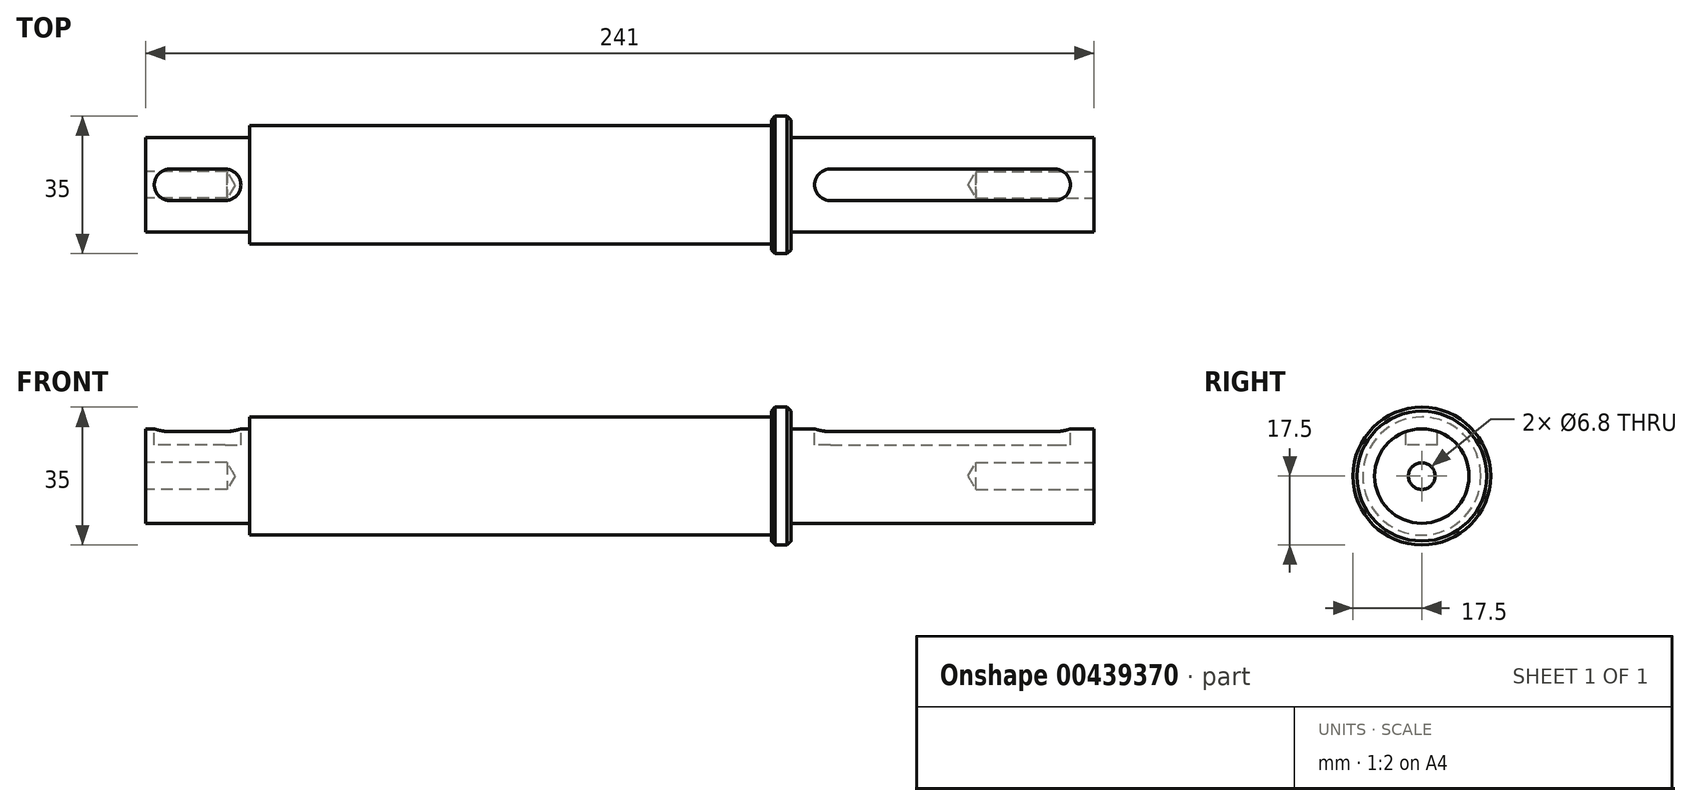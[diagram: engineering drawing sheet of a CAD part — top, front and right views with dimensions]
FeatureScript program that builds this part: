
annotation { "Feature Type Name" : "Feature", "Feature Type Description" : "" }
export const myFeature = defineFeature(function(context is Context, id is Id, definition is map)
    precondition{}
    {
        {
            var Q0;
            Q0=qCreatedBy(makeId("Right.planeOp"),FACE);
            var sketch = newSketch(context, id + "F0", { "sketchPlane" : qUnion([Q0])});
            skCircle(sketch, "E0", {"center": v(0, 0) * mm, "radius": 15 * mm});
            skSolve(sketch);
        }
        {
            var Q0;
            Q0=makeQuery(id+"F0.imprint","IMPRINT",FACE,{"disambiguationData":[TD([[makeQuery(id+"F0.imprint","IMPRINT",EDGE,{"derivedFrom":sQuery(id+"F0.wireOp",EDGE,"E0")}),1.0]])]});
            var Q1;
            Q1=makeQuery(id+"F0.imprint","IMPRINT",FACE,{"disambiguationData":[TD([[makeQuery(id+"F0.imprint","IMPRINT",EDGE,{"derivedFrom":sQuery(id+"F0.wireOp",EDGE,"RhCFtK50-c6vQ-g7bE-hiMF-q4ca7MKHe77k")}),1.0]])]});
            extrude(context, id + "F1", {"entities" : qUnion([Q0, Q1]), "depth" : 164 * mm});
        }
        {
            var Q0;
            Q0=makeQuery(id+"F1.opExtrude","CAP_FACE",FACE,{"disambiguationData":[OSD([sQuery(id+"F0.wireOp",EDGE,"E0")])],"isStart":false});
            var sketch = newSketch(context, id + "F2", { "sketchPlane" : qUnion([Q0])});
            skCircle(sketch, "E1", {"center": v(0, 0) * mm, "radius": 12 * mm});
            skSolve(sketch);
        }
        {
            var Q0;
            Q0=qSketchRegion(id+"F2",true);
            extrude(context, id + "F3", {"entities" : qUnion([Q0]), "operationType" : NewBodyOperationType.ADD, "depth" : 77 * mm});
        }
        {
            var Q0;
            Q0=makeQuery(id+"F3.opExtrude","CAP_FACE",FACE,{"disambiguationData":[OSD([sQuery(id+"F2.wireOp",EDGE,"E1")])],"isStart":false});
            var sketch = newSketch(context, id + "F4", { "sketchPlane" : qUnion([Q0])});
            skPoint(sketch, "E2", {"position": v(0, 0) * mm});
            skSolve(sketch);
        }
        {
            var Q0;
            Q0=sQuery(id+"F4.wireOp",VERTEX,"E2");
            var Q1;
            Q1=makeQuery(id+"F1.opExtrude","SWEPT_BODY",BODY,{"disambiguationData":[OSD([sQuery(id+"F0.wireOp",EDGE,"E0")])]});
            hole(context, id + "F5", {"style" : HoleStyle.SIMPLE, "endStyle" : HoleEndStyle.BLIND, "standardTappedOrClearance" : lookupTablePath({ "standard" : "ISO", "engagement" : "75%", "pitch" : "1.25 mm", "size" : "M8", "type" : "Tapped" }), "standardBlindInLast" : lookupTablePath({ "standard" : "ISO", "engagement" : "75%", "pitch" : "1.25 mm", "size" : "M8", "type" : "Tapped" }), "holeDiameter" : 6.8 * mm, "showTappedDepth" : true, "holeDepth" : 30 * mm, "isTappedThrough" : true, "tappedDepth" : 26.25 * mm, "tapClearance" : 3, "locations" : qUnion([Q0]), "scope" : qUnion([Q1]), "majorDiameter" : 8 * mm});
        }
        {
            var Q0;
            Q0=qCreatedBy(makeId("Top.planeOp"),FACE);
            cPlane(context, id + "F6", {"entities" : qUnion([Q0]), "cplaneType" : CPlaneType.OFFSET, "offset" : 12 * mm, "width" : 150 * mm, "height" : 150 * mm});
        }
        {
            var Q0;
            Q0=qCreatedBy(id+"F6.planeOp",FACE);
            var sketch = newSketch(context, id + "F7", { "sketchPlane" : qUnion([Q0])});
            skLineSegment(sketch, "E3", {"start": v(0, 0) * mm, "end": v(202.5, 0) * mm, "construction": true});
            skLineSegment(sketch, "E4.bottom", {"start": v(174, -4) * mm, "end": v(231, -4) * mm});
            skLineSegment(sketch, "E4.top", {"start": v(174, 4) * mm, "end": v(231, 4) * mm});
            skLineSegment(sketch, "E4.left", {"start": v(170, 0) * mm, "end": v(170, 0) * mm});
            skLineSegment(sketch, "E4.right", {"start": v(235, 0) * mm, "end": v(235, 0) * mm});
            skPoint(sketch, "E4.middle", {"position": v(202.5, 0) * mm});
            skPoint(sketch, "E5.visualSharp", {"position": v(170, -4) * mm});
            skArc(sketch, "E5.filletArc", {"start": v(170, 0) * mm, "mid": v(171.17, -2.83) * mm, "end": v(174, -4) * mm});
            skPoint(sketch, "E6.visualSharp", {"position": v(170, 4) * mm});
            skArc(sketch, "E6.filletArc", {"start": v(174, 4) * mm, "mid": v(171.17, 2.83) * mm, "end": v(170, 0) * mm});
            skPoint(sketch, "E7.visualSharp", {"position": v(235, 4) * mm});
            skArc(sketch, "E7.filletArc", {"start": v(235, 0) * mm, "mid": v(233.83, 2.83) * mm, "end": v(231, 4) * mm});
            skPoint(sketch, "E8.visualSharp", {"position": v(235, -4) * mm});
            skArc(sketch, "E8.filletArc", {"start": v(231, -4) * mm, "mid": v(233.83, -2.83) * mm, "end": v(235, 0) * mm});
            skSolve(sketch);
        }
        {
            var Q0;
            Q0=makeQuery(id+"F7.imprint","IMPRINT",FACE,{"disambiguationData":[TD([[makeQuery(id+"F7.imprint","IMPRINT",EDGE,{"derivedFrom":sQuery(id+"F7.wireOp",EDGE,"E4.bottom")}),1.0]])]});
            extrude(context, id + "F8", {"entities" : qUnion([Q0]), "operationType" : NewBodyOperationType.REMOVE, "oppositeDirection" : true, "depth" : 4.1 * mm});
        }
        {
            var Q0;
            Q0=makeQuery(id+"F1.opExtrude","CAP_FACE",FACE,{"disambiguationData":[OSD([sQuery(id+"F0.wireOp",EDGE,"E0")])],"isStart":false});
            var sketch = newSketch(context, id + "F9", { "sketchPlane" : qUnion([Q0])});
            skCircle(sketch, "E9", {"center": v(0, 0) * mm, "radius": 17.5 * mm});
            skCircle(sketch, "E10.0", {"center": v(0, 0) * mm, "radius": 15 * mm});
            skSolve(sketch);
        }
        {
            var Q0;
            Q0=makeQuery(id+"F9.imprint","IMPRINT",FACE,{"disambiguationData":[TD([[makeQuery(id+"F9.imprint","IMPRINT",EDGE,{"derivedFrom":sQuery(id+"F9.wireOp",EDGE,"E9")}),1.0]])]});
            extrude(context, id + "F10", {"entities" : qUnion([Q0]), "operationType" : NewBodyOperationType.ADD, "oppositeDirection" : true, "depth" : 5 * mm});
        }
        {
            var Q0;
            Q0=makeQuery(id+"F10.opExtrude","CAP_EDGE",EDGE,{"disambiguationData":[OSD([sQuery(id+"F9.wireOp",EDGE,"E9")])],"isStart":true});
            var Q1;
            Q1=makeQuery(id+"F10.opExtrude","CAP_EDGE",EDGE,{"disambiguationData":[OSD([sQuery(id+"F9.wireOp",EDGE,"E9")])],"isStart":false});
            chamfer(context, id + "F11", {"entities" : qUnion([Q0, Q1]), "width" : 1 * mm, "tangentPropagation" : true});
        }
        {
            var Q0;
            Q0=makeQuery(id+"F1.opExtrude","CAP_FACE",FACE,{"disambiguationData":[OSD([sQuery(id+"F0.wireOp",EDGE,"E0")])],"isStart":true});
            var sketch = newSketch(context, id + "F12", { "sketchPlane" : qUnion([Q0])});
            skCircle(sketch, "E11", {"center": v(0, 0) * mm, "radius": 15 * mm});
            skCircle(sketch, "E12", {"center": v(0, 0) * mm, "radius": 12 * mm});
            skSolve(sketch);
        }
        {
            var Q0;
            Q0=makeQuery(id+"F12.imprint","IMPRINT",FACE,{"disambiguationData":[TD([[makeQuery(id+"F12.imprint","IMPRINT",EDGE,{"derivedFrom":sQuery(id+"F12.wireOp",EDGE,"E11")}),-1.0]])]});
            extrude(context, id + "F13", {"entities" : qUnion([Q0]), "operationType" : NewBodyOperationType.REMOVE, "oppositeDirection" : true, "depth" : 26.5 * mm});
        }
        {
            var Q0;
            Q0=sQuery(id+"F12.wireOp",VERTEX,"E11.center");
            var Q1;
            Q1=makeQuery(id+"F1.opExtrude","SWEPT_BODY",BODY,{"disambiguationData":[OSD([sQuery(id+"F0.wireOp",EDGE,"E0")])]});
            hole(context, id + "F14", {"style" : HoleStyle.SIMPLE, "endStyle" : HoleEndStyle.BLIND, "standardTappedOrClearance" : lookupTablePath({ "standard" : "ISO", "engagement" : "75%", "pitch" : "1.25 mm", "size" : "M8", "type" : "Tapped" }), "standardBlindInLast" : lookupTablePath({ "standard" : "ISO", "engagement" : "75%", "pitch" : "1.25 mm", "size" : "M8", "type" : "Tapped" }), "holeDiameter" : 6.8 * mm, "showTappedDepth" : true, "holeDepth" : 20.75 * mm, "isTappedThrough" : true, "tappedDepth" : 17 * mm, "tapClearance" : 3, "locations" : qUnion([Q0]), "scope" : qUnion([Q1]), "majorDiameter" : 8 * mm});
        }
        {
            var Q0;
            Q0=qCreatedBy(id+"F6.planeOp",FACE);
            var sketch = newSketch(context, id + "F15", { "sketchPlane" : qUnion([Q0])});
            skLineSegment(sketch, "E13", {"start": v(0, 0) * mm, "end": v(26.5, 0) * mm, "construction": true});
            skPoint(sketch, "E14", {"position": v(13.25, 0) * mm});
            skLineSegment(sketch, "E15.bottom", {"start": v(20.25, -4) * mm, "end": v(6.25, -4) * mm});
            skLineSegment(sketch, "E15.top", {"start": v(20.25, 4) * mm, "end": v(6.25, 4) * mm});
            skLineSegment(sketch, "E15.left", {"start": v(24.25, 0) * mm, "end": v(24.25, 0) * mm});
            skLineSegment(sketch, "E15.right", {"start": v(2.25, 0) * mm, "end": v(2.25, 0) * mm});
            skPoint(sketch, "E16.visualSharp", {"position": v(2.25, 4) * mm});
            skArc(sketch, "E16.filletArc", {"start": v(6.25, 4) * mm, "mid": v(3.42, 2.83) * mm, "end": v(2.25, 0) * mm});
            skPoint(sketch, "E17.visualSharp", {"position": v(2.25, -4) * mm});
            skArc(sketch, "E17.filletArc", {"start": v(2.25, 0) * mm, "mid": v(3.42, -2.83) * mm, "end": v(6.25, -4) * mm});
            skPoint(sketch, "E18.visualSharp", {"position": v(24.25, -4) * mm});
            skArc(sketch, "E18.filletArc", {"start": v(20.25, -4) * mm, "mid": v(23.08, -2.83) * mm, "end": v(24.25, 0) * mm});
            skPoint(sketch, "E19.visualSharp", {"position": v(24.25, 4) * mm});
            skArc(sketch, "E19.filletArc", {"start": v(24.25, 0) * mm, "mid": v(23.08, 2.83) * mm, "end": v(20.25, 4) * mm});
            skSolve(sketch);
        }
        {
            var Q0;
            Q0=makeQuery(id+"F15.imprint","IMPRINT",FACE,{"disambiguationData":[TD([[makeQuery(id+"F15.imprint","IMPRINT",EDGE,{"derivedFrom":sQuery(id+"F15.wireOp",EDGE,"E15.bottom")}),-1.0]])]});
            extrude(context, id + "F16", {"entities" : qUnion([Q0]), "operationType" : NewBodyOperationType.REMOVE, "oppositeDirection" : true, "depth" : 4.1 * mm});
        }
    });
